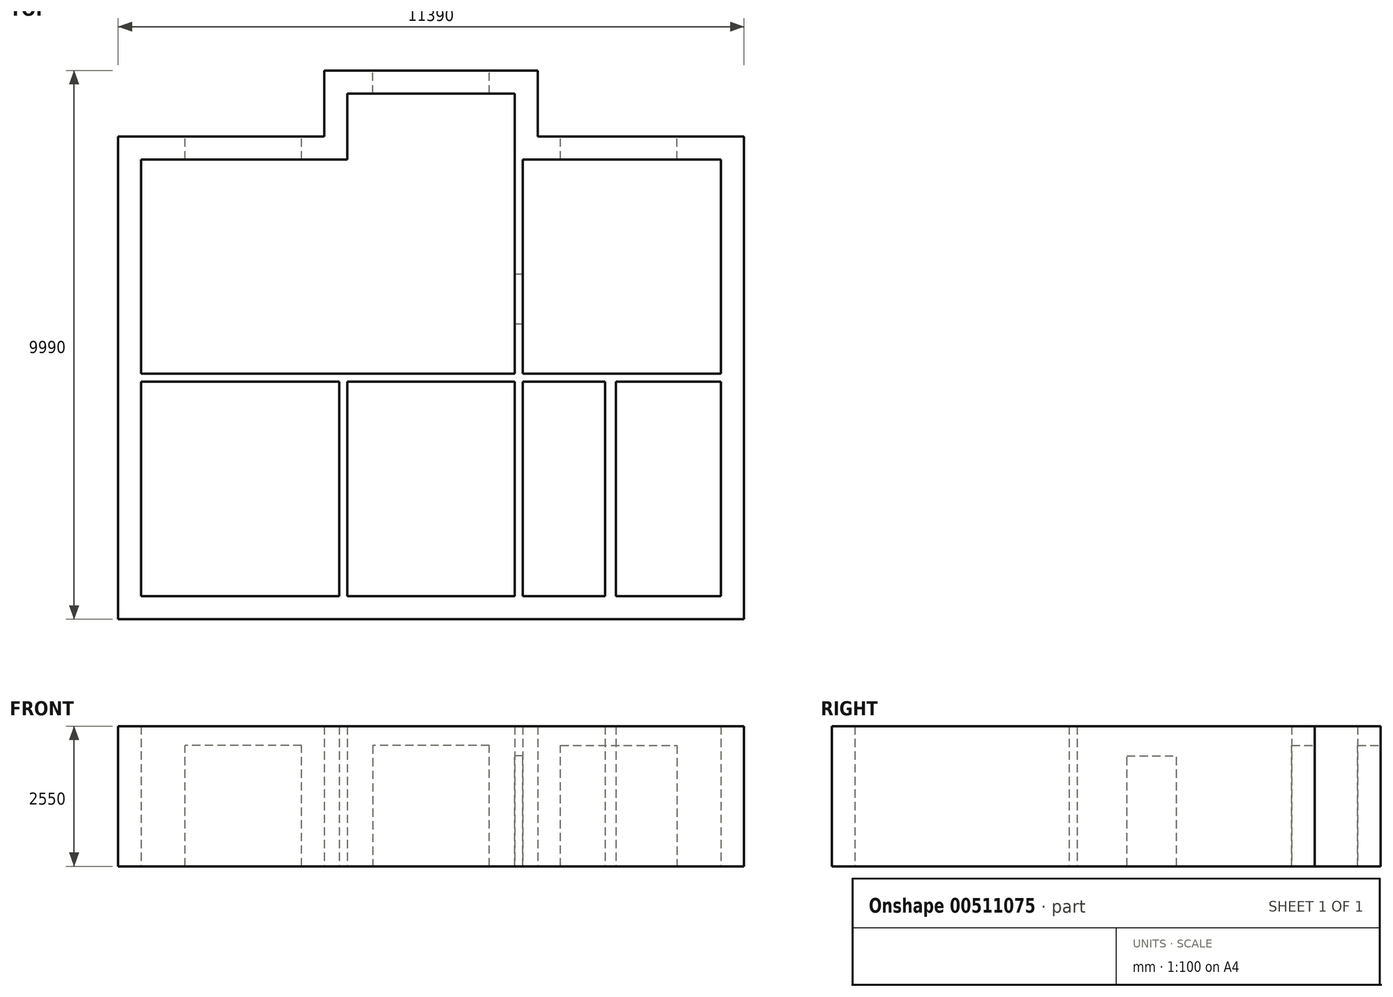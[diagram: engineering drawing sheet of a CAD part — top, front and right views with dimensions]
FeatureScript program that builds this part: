
annotation { "Feature Type Name" : "Feature", "Feature Type Description" : "" }
export const myFeature = defineFeature(function(context is Context, id is Id, definition is map)
    precondition{}
    {
        {
            var Q0;
            Q0=qCreatedBy(makeId("Top.planeOp"),FACE);
            var sketch = newSketch(context, id + "F0", { "sketchPlane" : qUnion([Q0])});
            skLineSegment(sketch, "E0", {"start": v(0, 0) * mm, "end": v(11390, 0) * mm});
            skLineSegment(sketch, "E1", {"start": v(11390, 0) * mm, "end": v(11390, 8790) * mm});
            skLineSegment(sketch, "E2", {"start": v(11390, 8790) * mm, "end": v(7637.5, 8790) * mm});
            skLineSegment(sketch, "E3", {"start": v(7637.5, 8790) * mm, "end": v(7637.5, 9990) * mm});
            skLineSegment(sketch, "E4", {"start": v(7637.5, 9990) * mm, "end": v(3752.5, 9990) * mm});
            skLineSegment(sketch, "E5", {"start": v(3752.5, 9990) * mm, "end": v(3752.5, 8790) * mm});
            skLineSegment(sketch, "E6", {"start": v(3752.5, 8790) * mm, "end": v(0, 8790) * mm});
            skLineSegment(sketch, "E7", {"start": v(0, 8790) * mm, "end": v(0, 0) * mm});
            skSolve(sketch);
        }
        {
            var Q0;
            Q0=makeQuery(id+"F0.imprint","IMPRINT",FACE,{"disambiguationData":[TD([[makeQuery(id+"F0.imprint","IMPRINT",EDGE,{"derivedFrom":sQuery(id+"F0.wireOp",EDGE,"E0")}),1.0]])]});
            var sketch = newSketch(context, id + "F1", { "sketchPlane" : qUnion([Q0])});
            skLineSegment(sketch, "E8", {"start": v(418, 8372) * mm, "end": v(4170.5, 8372) * mm});
            skLineSegment(sketch, "E9", {"start": v(4170.5, 8372) * mm, "end": v(4170.5, 9572) * mm});
            skLineSegment(sketch, "E10", {"start": v(4170.5, 9572) * mm, "end": v(7219.5, 9572) * mm});
            skLineSegment(sketch, "E11", {"start": v(7219.5, 9572) * mm, "end": v(7219.5, 4467) * mm});
            skLineSegment(sketch, "E12", {"start": v(7219.5, 4467) * mm, "end": v(418, 4467) * mm});
            skLineSegment(sketch, "E13", {"start": v(418, 4467) * mm, "end": v(418, 8372) * mm});
            skLineSegment(sketch, "E14.bottom", {"start": v(7364, 8372) * mm, "end": v(10972, 8372) * mm});
            skLineSegment(sketch, "E14.top", {"start": v(7364, 4467) * mm, "end": v(10972, 4467) * mm});
            skLineSegment(sketch, "E14.left", {"start": v(7364, 8372) * mm, "end": v(7364, 4467) * mm});
            skLineSegment(sketch, "E14.right", {"start": v(10972, 8372) * mm, "end": v(10972, 4467) * mm});
            skSolve(sketch);
        }
        {
            var Q0;
            Q0=makeQuery(id+"F0.imprint","IMPRINT",FACE,{"disambiguationData":[TD([[makeQuery(id+"F0.imprint","IMPRINT",EDGE,{"derivedFrom":sQuery(id+"F0.wireOp",EDGE,"E0")}),1.0]])]});
            extrude(context, id + "F2", {"entities" : qUnion([Q0]), "depth" : 2550 * mm});
        }
        {
            var Q0;
            Q0 = qSketchRegion(id + "F1", true);
            extrude(context, id + "F3", {"entities" : qUnion([Q0]), "operationType" : NewBodyOperationType.REMOVE, "depth" : 2550 * mm});
        }
        {
            var Q0;
            Q0=makeQuery(id+"F2.opExtrude","SWEPT_FACE",FACE,{"disambiguationData":[OSD([sQuery(id+"F0.wireOp",EDGE,"E2")])]});
            var sketch = newSketch(context, id + "F4", { "sketchPlane" : qUnion([Q0])});
            skLineSegment(sketch, "E15", {"start": v(-8052, 0) * mm, "end": v(-8052, 2200) * mm});
            skLineSegment(sketch, "E16", {"start": v(-8052, 2200) * mm, "end": v(-10172, 2200) * mm});
            skLineSegment(sketch, "E17", {"start": v(-10172, 2200) * mm, "end": v(-10172, 0) * mm});
            skLineSegment(sketch, "E18", {"start": v(-10172, 0) * mm, "end": v(-8052, 0) * mm});
            skSolve(sketch);
        }
        {
            var Q0;
            Q0=makeQuery(id+"F4.imprint","IMPRINT",FACE,{"disambiguationData":[TD([[makeQuery(id+"F4.imprint","IMPRINT",EDGE,{"derivedFrom":sQuery(id+"F4.wireOp",EDGE,"E15")}),1.0]])]});
            extrude(context, id + "F5", {"entities" : qUnion([Q0]), "operationType" : NewBodyOperationType.REMOVE, "oppositeDirection" : true, "depth" : 418 * mm});
        }
        {
            var Q0;
            Q0=makeQuery(id+"F2.opExtrude","SWEPT_FACE",FACE,{"disambiguationData":[OSD([sQuery(id+"F0.wireOp",EDGE,"E4")])]});
            var sketch = newSketch(context, id + "F6", { "sketchPlane" : qUnion([Q0])});
            skLineSegment(sketch, "E19", {"start": v(-6755.5, 0) * mm, "end": v(-6755.5, 2200) * mm});
            skLineSegment(sketch, "E20", {"start": v(-6755.5, 2200) * mm, "end": v(-4635.5, 2200) * mm});
            skLineSegment(sketch, "E21", {"start": v(-4635.5, 2200) * mm, "end": v(-4635.5, 0) * mm});
            skLineSegment(sketch, "E22", {"start": v(-4635.5, 0) * mm, "end": v(-6755.5, 0) * mm});
            skSolve(sketch);
        }
        {
            var Q0;
            Q0=makeQuery(id+"F6.imprint","IMPRINT",FACE,{"disambiguationData":[TD([[makeQuery(id+"F6.imprint","IMPRINT",EDGE,{"derivedFrom":sQuery(id+"F6.wireOp",EDGE,"E19")}),-1.0]])]});
            extrude(context, id + "F7", {"entities" : qUnion([Q0]), "operationType" : NewBodyOperationType.REMOVE, "oppositeDirection" : true, "depth" : 418 * mm});
        }
        {
            var Q0;
            Q0=makeQuery(id+"F2.opExtrude","SWEPT_FACE",FACE,{"disambiguationData":[OSD([sQuery(id+"F0.wireOp",EDGE,"E6")])]});
            var sketch = newSketch(context, id + "F8", { "sketchPlane" : qUnion([Q0])});
            skLineSegment(sketch, "E23.bottom", {"start": v(-3338, 0) * mm, "end": v(-1218, 0) * mm});
            skLineSegment(sketch, "E23.top", {"start": v(-3338, 2200) * mm, "end": v(-1218, 2200) * mm});
            skLineSegment(sketch, "E23.left", {"start": v(-3338, 0) * mm, "end": v(-3338, 2200) * mm});
            skLineSegment(sketch, "E23.right", {"start": v(-1218, 0) * mm, "end": v(-1218, 2200) * mm});
            skSolve(sketch);
        }
        {
            var Q0;
            Q0 = qSketchRegion(id + "F8", true);
            extrude(context, id + "F9", {"entities" : qUnion([Q0]), "operationType" : NewBodyOperationType.REMOVE, "oppositeDirection" : true, "depth" : 418 * mm});
        }
        {
            var Q0;
            Q0=makeQuery(id+"F3.boolean.opBoolean","COPY",FACE,{"derivedFrom":makeQuery(id+"F3.opExtrude","SWEPT_FACE",FACE,{"disambiguationData":[OSD([sQuery(id+"F1.wireOp",EDGE,"E11")])]})});
            var sketch = newSketch(context, id + "F10", { "sketchPlane" : qUnion([Q0])});
            skLineSegment(sketch, "E24.bottom", {"start": v(-5372, 0) * mm, "end": v(-6277, 0) * mm});
            skLineSegment(sketch, "E24.top", {"start": v(-5372, 2010) * mm, "end": v(-6277, 2010) * mm});
            skLineSegment(sketch, "E24.left", {"start": v(-5372, 0) * mm, "end": v(-5372, 2010) * mm});
            skLineSegment(sketch, "E24.right", {"start": v(-6277, 0) * mm, "end": v(-6277, 2010) * mm});
            skSolve(sketch);
        }
        {
            var Q0;
            Q0=makeQuery(id+"F10.imprint","IMPRINT",FACE,{"disambiguationData":[TD([[makeQuery(id+"F10.imprint","IMPRINT",EDGE,{"derivedFrom":sQuery(id+"F10.wireOp",EDGE,"E24.bottom")}),1.0]])]});
            extrude(context, id + "F11", {"entities" : qUnion([Q0]), "operationType" : NewBodyOperationType.REMOVE, "endBound" : BoundingType.UP_TO_NEXT, "oppositeDirection" : true, "depth" : 25 * mm});
        }
        {
            var Q0;
            Q0=qCreatedBy(makeId("Top.planeOp"),FACE);
            var sketch = newSketch(context, id + "F12", { "sketchPlane" : qUnion([Q0])});
            skLineSegment(sketch, "E25.bottom", {"start": v(418, 418) * mm, "end": v(4026, 418) * mm});
            skLineSegment(sketch, "E25.top", {"start": v(418, 4322) * mm, "end": v(4026, 4322) * mm});
            skLineSegment(sketch, "E25.left", {"start": v(418, 418) * mm, "end": v(418, 4322) * mm});
            skLineSegment(sketch, "E25.right", {"start": v(4026, 418) * mm, "end": v(4026, 4322) * mm});
            skLineSegment(sketch, "E26.bottom", {"start": v(4171, 4322) * mm, "end": v(7221, 4322) * mm});
            skLineSegment(sketch, "E26.top", {"start": v(4171, 418) * mm, "end": v(7221, 418) * mm});
            skLineSegment(sketch, "E26.left", {"start": v(4171, 4322) * mm, "end": v(4171, 418) * mm});
            skLineSegment(sketch, "E26.right", {"start": v(7221, 4322) * mm, "end": v(7221, 418) * mm});
            skLineSegment(sketch, "E27.bottom", {"start": v(7366, 4322) * mm, "end": v(8866, 4322) * mm});
            skLineSegment(sketch, "E27.top", {"start": v(7366, 418) * mm, "end": v(8866, 418) * mm});
            skLineSegment(sketch, "E27.left", {"start": v(7366, 4322) * mm, "end": v(7366, 418) * mm});
            skLineSegment(sketch, "E27.right", {"start": v(8866, 4322) * mm, "end": v(8866, 418) * mm});
            skLineSegment(sketch, "E28.bottom", {"start": v(9061, 4322) * mm, "end": v(10974, 4322) * mm});
            skLineSegment(sketch, "E28.top", {"start": v(9061, 418) * mm, "end": v(10974, 418) * mm});
            skLineSegment(sketch, "E28.left", {"start": v(9061, 4322) * mm, "end": v(9061, 418) * mm});
            skLineSegment(sketch, "E28.right", {"start": v(10974, 4322) * mm, "end": v(10974, 418) * mm});
            skSolve(sketch);
        }
        {
            var Q0;
            Q0 = qSketchRegion(id + "F12", true);
            extrude(context, id + "F13", {"entities" : qUnion([Q0]), "operationType" : NewBodyOperationType.REMOVE, "endBound" : BoundingType.THROUGH_ALL, "depth" : 25 * mm});
        }
    });
